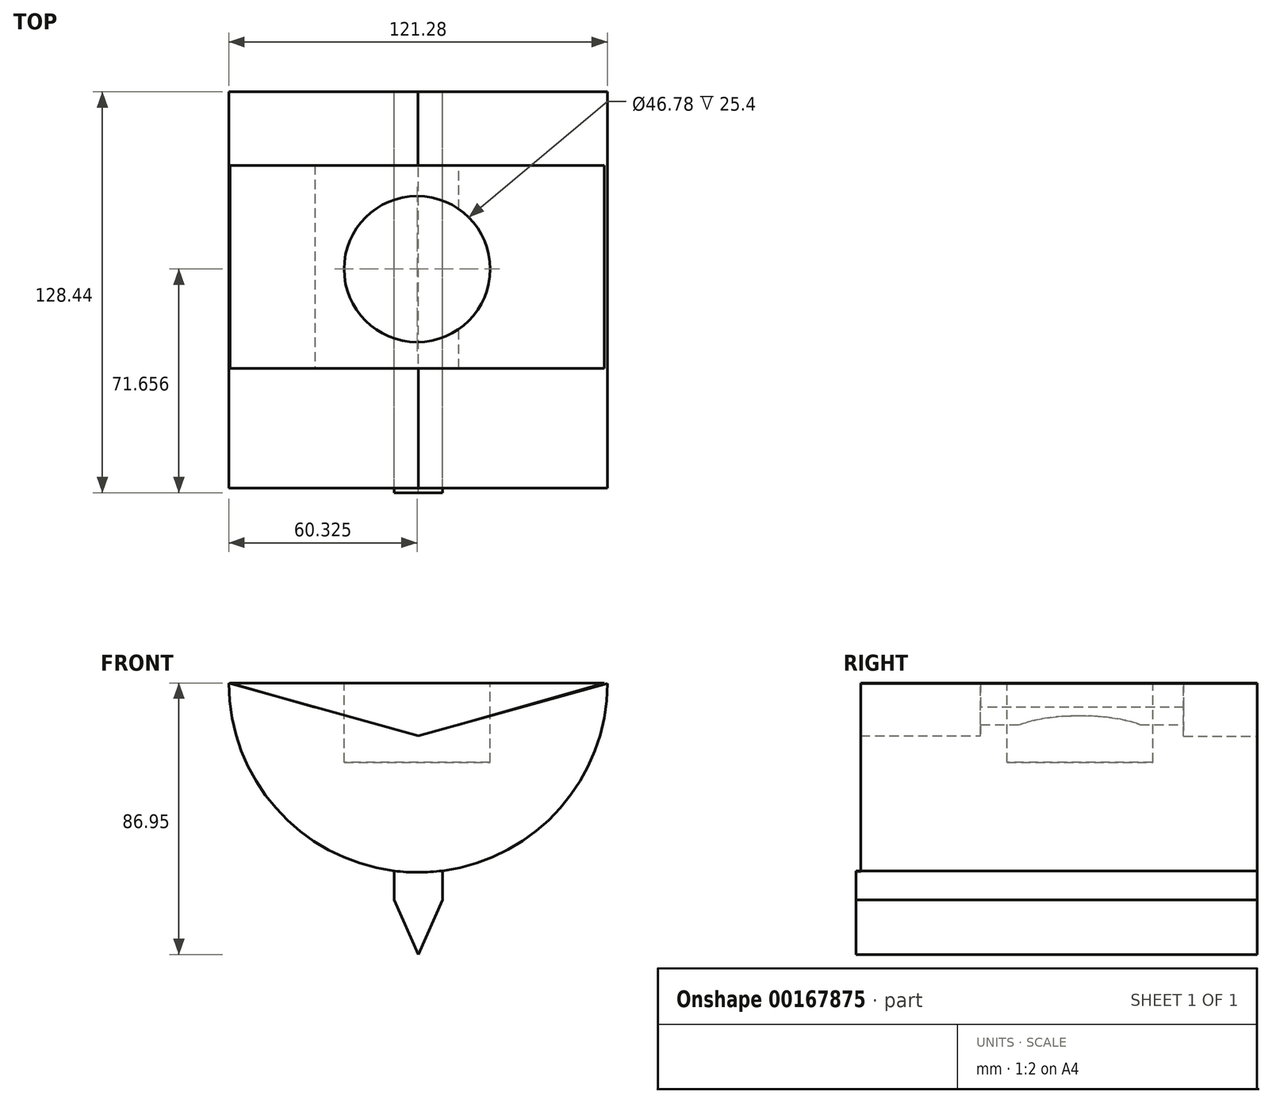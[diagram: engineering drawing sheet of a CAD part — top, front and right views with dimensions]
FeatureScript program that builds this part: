
annotation { "Feature Type Name" : "Feature", "Feature Type Description" : "" }
export const myFeature = defineFeature(function(context is Context, id is Id, definition is map)
    precondition{}
    {
        {
            var Q0;
            Q0=qCreatedBy(makeId("Front.planeOp"),FACE);
            var sketch = newSketch(context, id + "F0", { "sketchPlane" : qUnion([Q0])});
            skArc(sketch, "E0", {"start": v(-60.64, 0) * mm, "mid": v(-0.04, -60.64) * mm, "end": v(60.64, -0.07) * mm});
            skLineSegment(sketch, "E1", {"start": v(-51.91, -31.35) * mm, "end": v(51.91, -31.35) * mm});
            skLineSegment(sketch, "E2", {"start": v(51.91, -31.35) * mm, "end": v(-60.64, 0) * mm});
            skLineSegment(sketch, "E3", {"start": v(60.64, -0.07) * mm, "end": v(-51.91, -31.35) * mm});
            skSolve(sketch);
        }
        {
            var Q0;
            Q0 = qSketchRegion(id + "F0", true);
            extrude(context, id + "F1", {"entities" : qUnion([Q0]), "depth" : 127 * mm});
        }
        {
            var Q0;
            Q0=makeQuery(id+"F1.opExtrude","CAP_FACE",FACE,{"disambiguationData":[OSD([sQuery(id+"F0.wireOp",EDGE,"E0"),sQuery(id+"F0.wireOp",EDGE,"E2"),sQuery(id+"F0.wireOp",EDGE,"E3")])],"isStart":true});
            var sketch = newSketch(context, id + "F2", { "sketchPlane" : qUnion([Q0])});
            skLineSegment(sketch, "E4.bottom", {"start": v(-7.8, -69.43) * mm, "end": v(7.7, -69.43) * mm});
            skLineSegment(sketch, "E4.top", {"start": v(-7.8, 35.62) * mm, "end": v(7.7, 35.62) * mm});
            skLineSegment(sketch, "E4.left", {"start": v(-7.8, -69.43) * mm, "end": v(-7.8, 35.62) * mm});
            skLineSegment(sketch, "E4.right", {"start": v(7.7, -69.43) * mm, "end": v(7.7, 35.62) * mm});
            skPoint(sketch, "E4.middle", {"position": v(-0.06, -16.9) * mm});
            skLineSegment(sketch, "E5", {"start": v(-7.8, -69.43) * mm, "end": v(-0.06, -86.95) * mm});
            skPoint(sketch, "E5.endSnap0", {"position": v(-0.06, -69.43) * mm});
            skLineSegment(sketch, "E6", {"start": v(-0.06, -86.95) * mm, "end": v(7.7, -69.43) * mm});
            skLineSegment(sketch, "E7", {"start": v(-7.8, -16.9) * mm, "end": v(7.7, -16.9) * mm});
            skSolve(sketch);
        }
        {
            var Q0;
            {var subQ0=sQuery(id+"F2.wireOp",EDGE,"E4.bottom");Q0=makeQuery(id+"F2.imprint","IMPRINT",FACE,{"disambiguationData":[TD([[makeQuery(id+"F2.imprint","IMPRINT",EDGE,{"derivedFrom":subQ0}),1.0]])]});}
            var Q1;
            Q1=makeQuery(id+"F2.imprint","IMPRINT",FACE,{"disambiguationData":[TD([[makeQuery(id+"F2.imprint","IMPRINT",EDGE,{"derivedFrom":sQuery(id+"F2.wireOp",EDGE,"E4.bottom")}),-1.0]])]});
            extrude(context, id + "F3", {"entities" : qUnion([Q0, Q1]), "operationType" : NewBodyOperationType.ADD, "oppositeDirection" : true, "depth" : 128.44 * mm});
        }
        {
            var Q0;
            Q0=qCreatedBy(makeId("Front.planeOp"),FACE);
            var sketch = newSketch(context, id + "F4", { "sketchPlane" : qUnion([Q0])});
            skLineSegment(sketch, "E8", {"start": v(0, 0) * mm, "end": v(0, -17.02) * mm});
            skLineSegment(sketch, "E9", {"start": v(0, -17.02) * mm, "end": v(59.63, 0) * mm});
            skLineSegment(sketch, "E10", {"start": v(59.63, 0) * mm, "end": v(0, 0) * mm});
            skLineSegment(sketch, "E11", {"start": v(-60.26, 0) * mm, "end": v(0, -17.02) * mm});
            skLineSegment(sketch, "E12", {"start": v(0, 0) * mm, "end": v(-60.26, 0) * mm});
            skSolve(sketch);
        }
        {
            var Q0;
            Q0 = qSketchRegion(id + "F4", true);
            extrude(context, id + "F5", {"entities" : qUnion([Q0]), "operationType" : NewBodyOperationType.ADD, "depth" : 88.56 * mm});
        }
        {
            var Q0;
            Q0=makeQuery(id+"F4.imprint","IMPRINT",FACE,{"disambiguationData":[TD([[makeQuery(id+"F4.imprint","IMPRINT",EDGE,{"derivedFrom":sQuery(id+"F4.wireOp",EDGE,"E8")}),1.0]])]});
            var Q1;
            Q1=makeQuery(id+"F4.imprint","IMPRINT",FACE,{"disambiguationData":[TD([[makeQuery(id+"F4.imprint","IMPRINT",EDGE,{"derivedFrom":sQuery(id+"F4.wireOp",EDGE,"E8")}),-1.0]])]});
            extrude(context, id + "F6", {"entities" : qUnion([Q0, Q1]), "operationType" : NewBodyOperationType.REMOVE, "depth" : 23.55 * mm});
        }
        {
            var Q0;
            Q0=makeQuery(id+"F5.opExtrude","SWEPT_FACE",FACE,{"disambiguationData":[OSD([sQuery(id+"F4.wireOp",EDGE,"E10"),sQuery(id+"F4.wireOp",EDGE,"E12")])]});
            var sketch = newSketch(context, id + "F7", { "sketchPlane" : qUnion([Q0])});
            skCircle(sketch, "E13", {"center": v(-0.31, -56.78) * mm, "radius": 23.4 * mm});
            skPoint(sketch, "E13.centerSnap0", {"position": v(-0.31, -23.55) * mm});
            skSolve(sketch);
        }
        {
            var Q0;
            Q0 = qSketchRegion(id + "F7", true);
            extrude(context, id + "F8", {"entities" : qUnion([Q0]), "operationType" : NewBodyOperationType.REMOVE, "oppositeDirection" : true, "depth" : 25.4 * mm});
        }
    });
